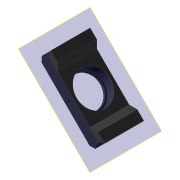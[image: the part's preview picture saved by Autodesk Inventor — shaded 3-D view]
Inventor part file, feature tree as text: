
AUTODESK INVENTOR PART (.ipt)
format: ipt  version: 2019.4 (Build 234330000, 330)  size: 195,072 bytes
history: native  units: mm
features: extrude x4, sketch x4, other x3, projected_geometry x3, plane x1
ambient origin geometry x8: Origin, YZ Plane, XZ Plane, XY Plane, X Axis, Y Axis, Z Axis, Center Point
bodies: Solid1 (feature_tree)
feature tree (15):
  other  "20_Cube_Insert_Mirror_Holder_wLogo_v3.ipt"
  extrude  "Extrusion1"  Depth=10.0mm
  extrude  "Extrusion2"  Depth=4.5mm TaperAngle=0.0deg
  extrude  "Extrusion3"  Depth=4.5mm TaperAngle=0.0deg
  extrude  "Extrusion4"  [1 undecoded]
  other  "Solid1::20_Cube_Insert_Mirror_Holder_wLogo_v3.ipt"
  other  "TaggingFeature1"
  plane  "Work Plane1"
  sketch  "Sketch1"  dims[d0=10.0mm d1=25.8mm]
  projected_geometry  "Projected Loop1"
  sketch  "Sketch2"  dims[d2=5.0mm d3=0.0mm d4=4.5mm d5=0.0mm]
  projected_geometry  "Projected Loop2"
  sketch  "Sketch3"  dims[d6=2.9mm d7=4.5mm d8=0.0mm]
  projected_geometry  "Projected Loop3"
  sketch  "Sketch4"  dims[d9=2.0mm d10=0.0mm]
note: 1 required parameter value undecoded (feature->parameter linkage not recoverable at this tier; creation-order binding heuristic only, values carry confidence <= 0.55)
